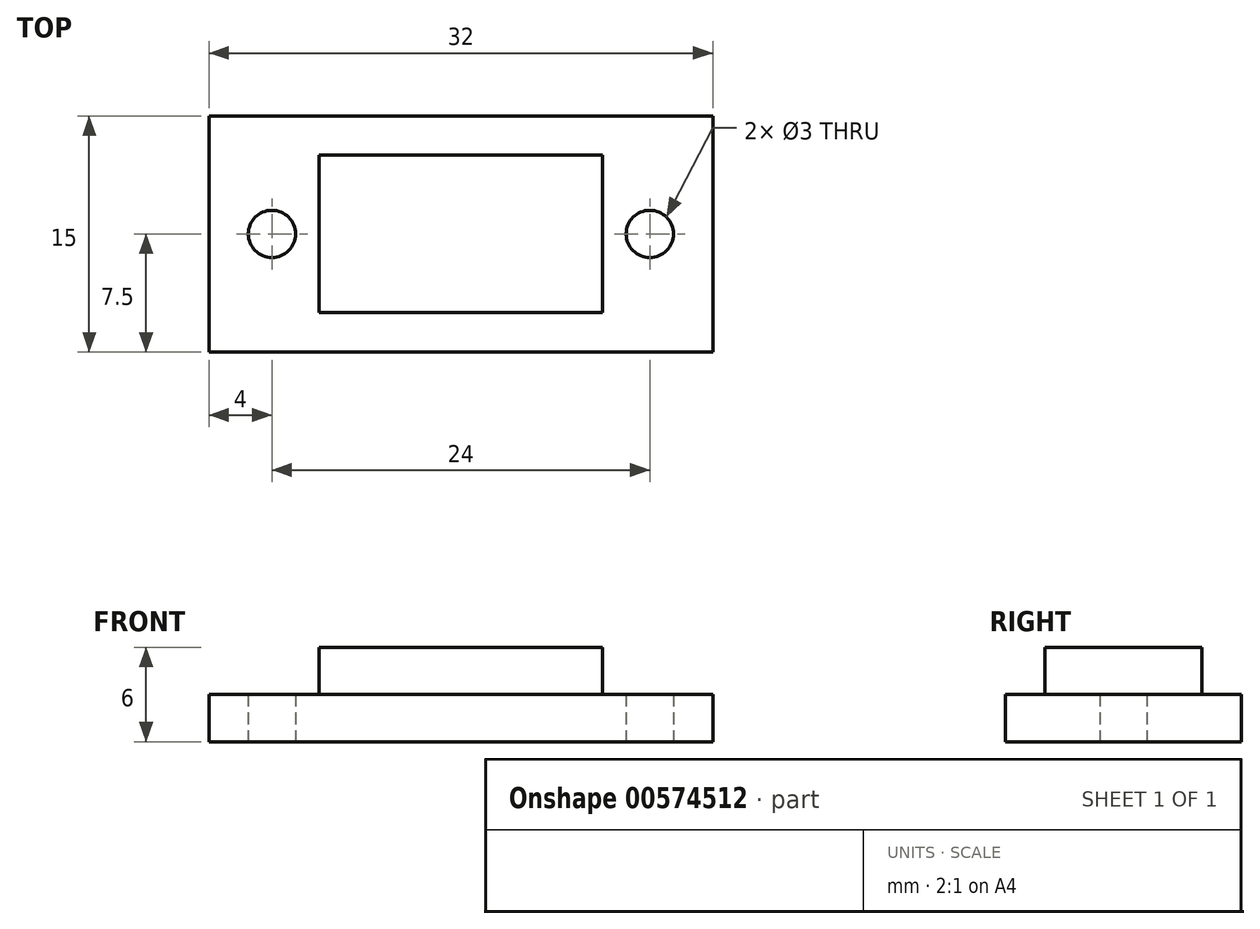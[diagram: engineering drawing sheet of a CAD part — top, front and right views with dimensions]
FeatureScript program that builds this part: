
annotation { "Feature Type Name" : "Feature", "Feature Type Description" : "" }
export const myFeature = defineFeature(function(context is Context, id is Id, definition is map)
    precondition{}
    {
        {
            var Q0;
            Q0=qCreatedBy(makeId("Top.planeOp"),FACE);
            var sketch = newSketch(context, id + "F0", { "sketchPlane" : qUnion([Q0])});
            skLineSegment(sketch, "E0.bottom", {"start": v(-16, 7.5) * mm, "end": v(16, 7.5) * mm});
            skLineSegment(sketch, "E0.top", {"start": v(-16, -7.5) * mm, "end": v(16, -7.5) * mm});
            skLineSegment(sketch, "E0.left", {"start": v(-16, 7.5) * mm, "end": v(-16, -7.5) * mm});
            skLineSegment(sketch, "E0.right", {"start": v(16, 7.5) * mm, "end": v(16, -7.5) * mm});
            skCircle(sketch, "E1", {"center": v(-12, 0) * mm, "radius": 1.5 * mm});
            skCircle(sketch, "E2", {"center": v(12, 0) * mm, "radius": 1.5 * mm});
            skSolve(sketch);
        }
        {
            var Q0;
            Q0=makeQuery(id+"F0.imprint","IMPRINT",FACE,{"disambiguationData":[TD([[makeQuery(id+"F0.imprint","IMPRINT",EDGE,{"derivedFrom":sQuery(id+"F0.wireOp",EDGE,"E0.bottom")}),-1.0]])]});
            extrude(context, id + "F1", {"entities" : qUnion([Q0]), "depth" : 3 * mm, "offsetDistance" : 25 * mm});
        }
        {
            var Q0;
            Q0=makeQuery(id+"F1.opExtrude","CAP_FACE",FACE,{"disambiguationData":[OSD([sQuery(id+"F0.wireOp",EDGE,"E0.bottom"),sQuery(id+"F0.wireOp",EDGE,"E0.top"),sQuery(id+"F0.wireOp",EDGE,"E0.left"),sQuery(id+"F0.wireOp",EDGE,"E0.right"),sQuery(id+"F0.wireOp",EDGE,"E1"),sQuery(id+"F0.wireOp",EDGE,"E2")])],"isStart":false});
            var sketch = newSketch(context, id + "F2", { "sketchPlane" : qUnion([Q0])});
            skLineSegment(sketch, "E3.0.0", {"start": v(-16, 7.5) * mm, "end": v(-16, -7.5) * mm});
            skLineSegment(sketch, "E3.0.1", {"start": v(-16, -7.5) * mm, "end": v(16, -7.5) * mm});
            skLineSegment(sketch, "E3.0.2", {"start": v(16, -7.5) * mm, "end": v(16, 7.5) * mm});
            skLineSegment(sketch, "E3.0.3", {"start": v(16, 7.5) * mm, "end": v(-16, 7.5) * mm});
            skLineSegment(sketch, "E4.bottom", {"start": v(-9, 5) * mm, "end": v(9, 5) * mm});
            skLineSegment(sketch, "E4.top", {"start": v(-9, -5) * mm, "end": v(9, -5) * mm});
            skLineSegment(sketch, "E4.left", {"start": v(-9, 5) * mm, "end": v(-9, -5) * mm});
            skLineSegment(sketch, "E4.right", {"start": v(9, 5) * mm, "end": v(9, -5) * mm});
            skSolve(sketch);
        }
        {
            var Q0;
            Q0=makeQuery(id+"F2.imprint","IMPRINT",FACE,{"disambiguationData":[TD([[makeQuery(id+"F2.imprint","IMPRINT",EDGE,{"derivedFrom":sQuery(id+"F2.wireOp",EDGE,"E4.bottom")}),-1.0]])]});
            extrude(context, id + "F3", {"entities" : qUnion([Q0]), "operationType" : NewBodyOperationType.ADD, "depth" : 3 * mm, "offsetDistance" : 25 * mm});
        }
    });
